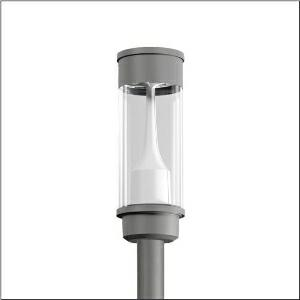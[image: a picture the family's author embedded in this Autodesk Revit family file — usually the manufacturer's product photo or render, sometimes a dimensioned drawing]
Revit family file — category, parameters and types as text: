
# Revit family: litepole_iq___p1_0a_5xa5415bf14h_51c2
name_source: partatom
category: Lighting Fixtures
units: mm (PartAtom-declared; Revit-internal decimal feet)

## family parameters
Cut with Voids When Loaded = No
Host = Face
Light Source = No
Part Type = Normal
Room Calculation Point = No
Round Connector Dimension = Use Diameter
Shared = No

## types (1)
- --- (1 x LED, 1510 lm, 12.9 W, 2200K)
    Apparent Load = 13 VA
    CIE Flux Codes = 32 61 90 93 100
    Color Rendering = 70
    Color Temperature = 2200K
    Default Elevation = 1800 mm
    Description = Litepole iQ, mast luminaire, Module 540 iQ-SR, primary light control with 3 zone facetted reflector, of plastic, silver coated, highly specular, structured, primary optical cover: cover, of PMMA, transparent, partly coated, light distribution: P1.0a, light emission: direct distribution, primary light characteristic: strongly asymmetric, installation type: post-top, LED, High Power LED, rated luminous flux: 1.510lm, luminous efficacy: 117lm/W, light colour: 722, colour temperature: 2200K, control gear: iQ Street-Remote, control: optimised constant luminous flux control (CLO 2.0), Desk-Remote (wireless, voltage-free reading and setting of iQ features in the workshop via application-optimized NFC function/RFID function), Light-Fading, Smart-Wire, Night-Set, Lumen-Switch, Temp-Guard, Auto-Match, Street-Remote, pre-setting: logarithmic dimming characteristic, with terminal, 6-pole, max. 2.5mm², mains connection: 230..240V, AC, 50/60Hz, start of lifetime: 13W, end of service life: 13W, reduction: 6W, luminaire housing, upper part, of glass-fibre reinforced polyester, coated, Siteco® metallic grey (DB 702S), diameter: 210mm, height: 590mm, spigot size: d x l = 76 x 70mm (post-top) | with reducer (optional accessory) 60 x 70mm, mounting height: 3..5m, post-top mast mounting element, of diecast aluminium, coated, Siteco® metallic grey (DB 702S), Module 540 iQ-SR, traffic white (RAL 9016), equipment: standard, protection rating (complete): IP65, insulation class (complete): insulation class II (safety insulation), certification: CE, ENEC, VDE, packaging unit: 1 piece

Light Distribution: P1.0a
    Height = 590 mm
    Lamp = 1 x LED
    Lamp Light Flux = 1510 lm
    Lamp Power = 12.9 W
    Lamp count = 1
    Length = 220 mm
    Luminous efficacy = 117 lm/W
    Manufacturer = Siteco
    ModVariant = No
    Model = 5XA5415BF14H
    Number of Poles = 1
    OnlyDefault = Yes
    Power Factor = 1
    Product Name = Litepole iQ | P1.0a
    Product group = mast luminaire | pylon top
    ProductGroupID = 6100
    Protection Class = Protection class II
    Protection Degree = IP 65
    RLX_Detail_Level = 1
    RLX_Emergency_Light_Flux = 0 lm
    RLX_Emergency_Type = 0
    RLX_Emergency_Type_DB = No
    RlxData = <blob elided: 64441 chars, md5=581ea7de>
    Socket = socket
    Standby Power = 0 W
    System Light Flux = 1510 lm
    System Power = 13 W
    Type Comments = factory setting: luminous flux: 100 % | dim-lin: 254 | 516 mA
    Type Image = l_1006025.jpg
    URL = http://relux.com
    VarID = @adj_180227
    Voltage = 0 V
    Weight = 0.00 kg
    Width = 0 mm  [stored 0 ft]

note: [stored X ft] marks values corroborated as IEEE doubles in the binary element streams (Revit-internal decimal feet)

## geometry (parser evidence)
native form markers: Blend x4, Sweep x12
no freeform markers — native parametric forms only
